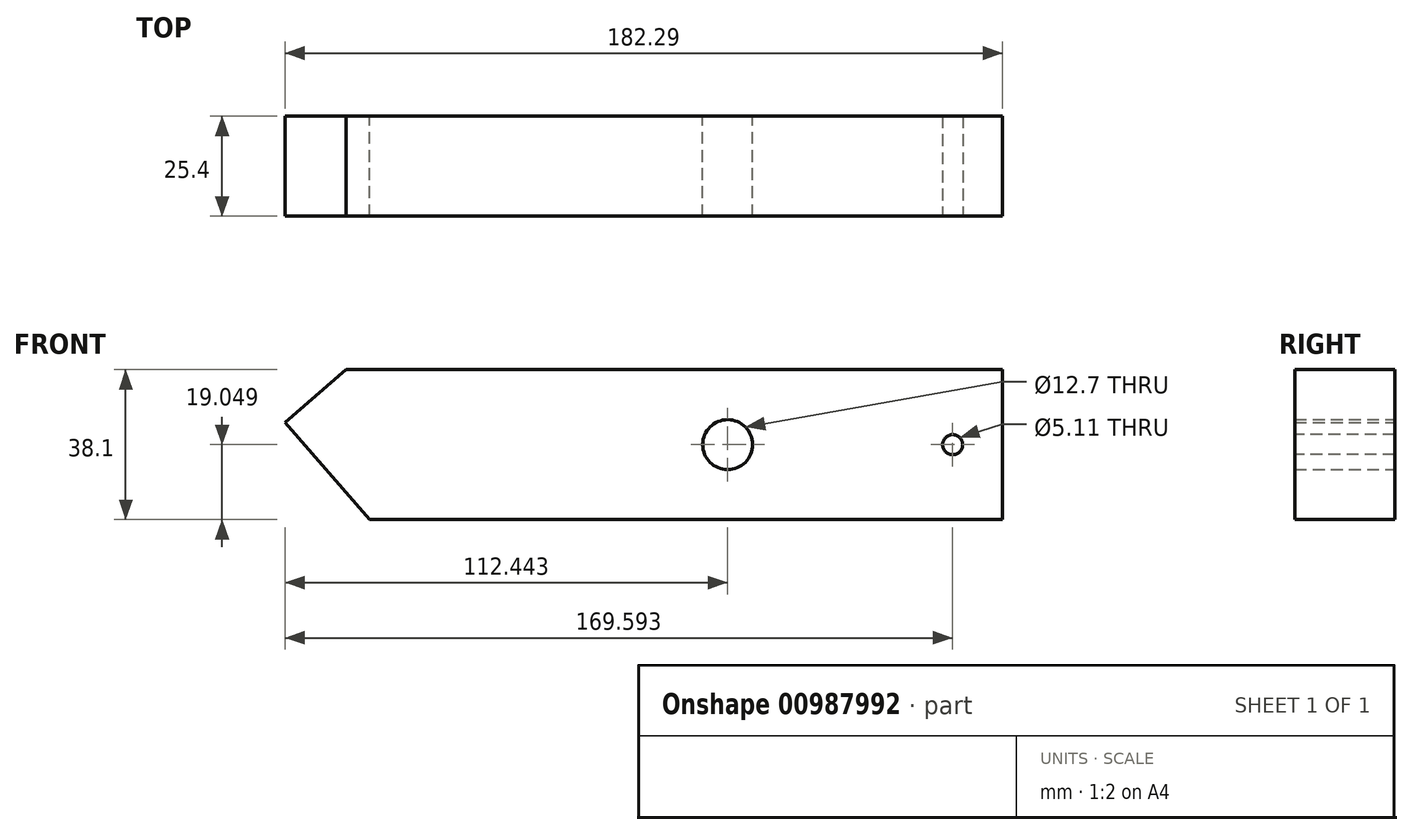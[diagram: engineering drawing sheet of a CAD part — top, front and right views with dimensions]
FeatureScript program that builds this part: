
annotation { "Feature Type Name" : "Feature", "Feature Type Description" : "" }
export const myFeature = defineFeature(function(context is Context, id is Id, definition is map)
    precondition{}
    {
        {
            var Q0;
            Q0=qCreatedBy(makeId("Front.planeOp"),FACE);
            var sketch = newSketch(context, id + "F0", { "sketchPlane" : qUnion([Q0])});
            skLineSegment(sketch, "E0.bottom", {"start": v(-77.24, 21.93) * mm, "end": v(89.55, 21.93) * mm});
            skLineSegment(sketch, "E0.top", {"start": v(-71.34, -16.17) * mm, "end": v(89.55, -16.17) * mm});
            skLineSegment(sketch, "E0.right", {"start": v(89.55, 21.93) * mm, "end": v(89.55, -16.17) * mm});
            skCircle(sketch, "E1", {"center": v(19.7, 2.88) * mm, "radius": 6.35 * mm});
            skPoint(sketch, "E1.centerSnap0", {"position": v(-121.72, 2.88) * mm});
            skLineSegment(sketch, "E2", {"start": v(-77.24, 21.93) * mm, "end": v(-92.74, 8.47) * mm});
            skLineSegment(sketch, "E3", {"start": v(-92.74, 8.47) * mm, "end": v(-71.34, -16.17) * mm});
            skSolve(sketch);
        }
        {
            var Q0;
            Q0=makeQuery(id+"F0.imprint","IMPRINT",FACE,{"disambiguationData":[TD([[makeQuery(id+"F0.imprint","IMPRINT",EDGE,{"derivedFrom":sQuery(id+"F0.wireOp",EDGE,"E0.bottom")}),-1.0]])]});
            extrude(context, id + "F1", {"entities" : qUnion([Q0]), "depth" : 25.4 * mm, "offsetDistance" : 25.4 * mm});
        }
        {
            var Q0;
            Q0=makeQuery(id+"F1.opExtrude","CAP_FACE",FACE,{"disambiguationData":[OSD([sQuery(id+"F0.wireOp",EDGE,"E0.bottom"),sQuery(id+"F0.wireOp",EDGE,"E0.top"),sQuery(id+"F0.wireOp",EDGE,"E0.right"),sQuery(id+"F0.wireOp",EDGE,"E1"),sQuery(id+"F0.wireOp",EDGE,"E2"),sQuery(id+"F0.wireOp",EDGE,"E3")])],"isStart":false});
            var sketch = newSketch(context, id + "F2", { "sketchPlane" : qUnion([Q0])});
            skPoint(sketch, "E4", {"position": v(76.85, 2.88) * mm});
            skPoint(sketch, "E4.positionSnap0", {"position": v(89.55, 2.88) * mm});
            skSolve(sketch);
        }
        {
            var Q0;
            Q0=sQuery(id+"F2.wireOp",VERTEX,"E4");
            var Q1;
            Q1=makeQuery(id+"F1.opExtrude","SWEPT_BODY",BODY,{"disambiguationData":[OSD([sQuery(id+"F0.wireOp",EDGE,"E0.bottom"),sQuery(id+"F0.wireOp",EDGE,"E0.top"),sQuery(id+"F0.wireOp",EDGE,"E0.right"),sQuery(id+"F0.wireOp",EDGE,"E1"),sQuery(id+"F0.wireOp",EDGE,"E2"),sQuery(id+"F0.wireOp",EDGE,"E3")])]});
            hole(context, id + "F3", {"style" : HoleStyle.SIMPLE, "endStyle" : HoleEndStyle.THROUGH, "standardTappedOrClearance" : lookupTablePath({ "standard" : "ANSI", "engagement" : "75%", "pitch" : "20 tpi", "size" : "1/4", "type" : "Tapped" }), "standardBlindInLast" : lookupTablePath({ "standard" : "ANSI", "fit" : "Normal", "engagement" : "75%", "pitch" : "20 tpi", "size" : "1/4", "type" : "Clearance & tapped" }), "holeDiameter" : 5.1 * mm, "majorDiameter" : 6.35 * mm, "showTappedDepth" : true, "isTappedThrough" : true, "tappedDepth" : 92.56 * mm, "tapClearance" : 3, "locations" : qUnion([Q0]), "scope" : qUnion([Q1])});
        }
    });
